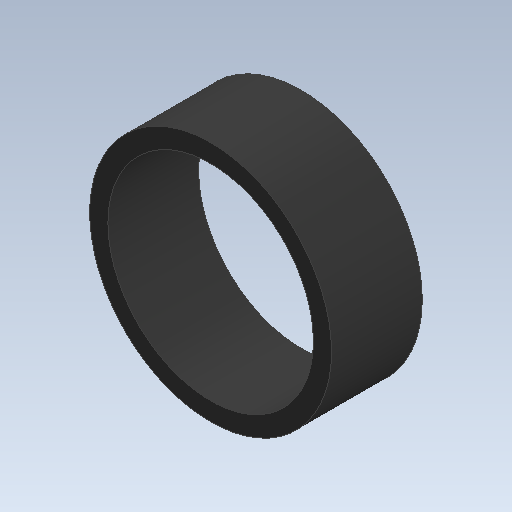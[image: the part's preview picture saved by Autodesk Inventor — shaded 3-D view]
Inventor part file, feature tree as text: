
AUTODESK INVENTOR PART (.ipt)
format: ipt  version: 2020 (Build 240168000, 168)  size: 99,840 bytes
history: native  units: in
note: dims shown in document units (in); Inventor stores cm internally (conversion verified against a paired STEP export)
features: extrude x1, sketch x1
ambient origin geometry x8: Origin, YZ Plane, XZ Plane, XY Plane, X Axis, Y Axis, Z Axis, Center Point
bodies: Solid1 (feature_tree)
feature tree (2):
  extrude  "Extrusion1"  Depth=1.5in
  sketch  "Sketch1"  dims[d0=3.4in d1=4.0in d2=1.5in d3=0.0in]
